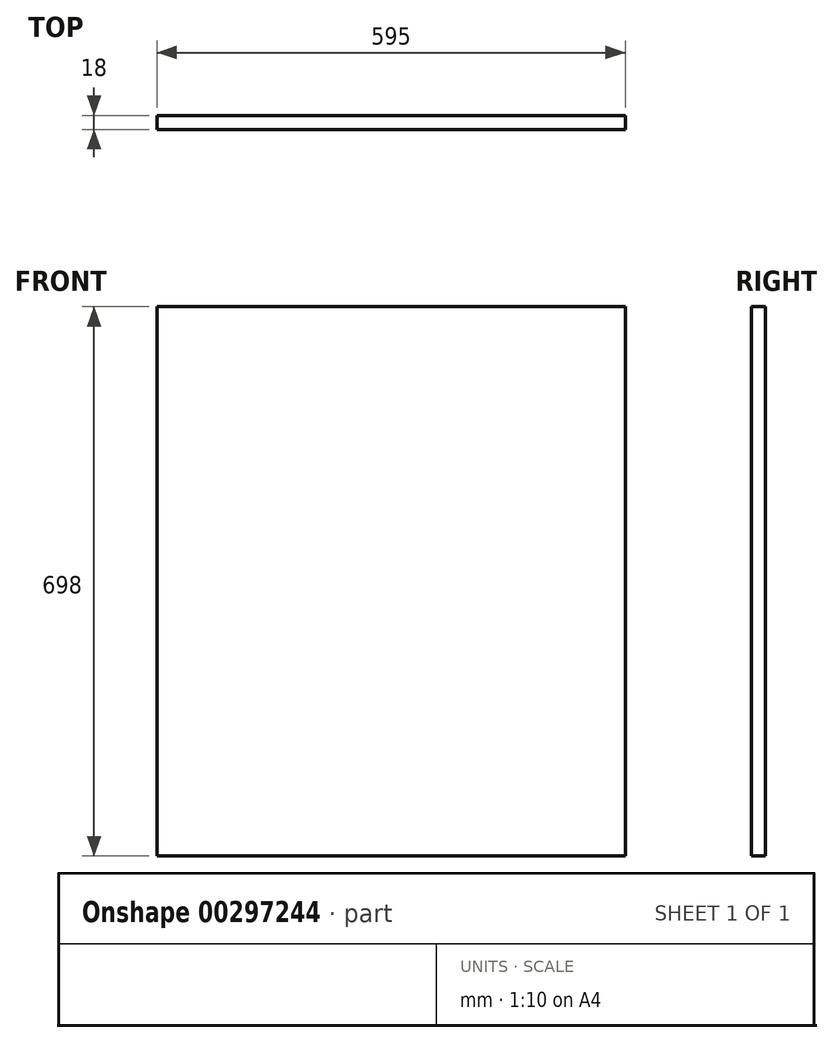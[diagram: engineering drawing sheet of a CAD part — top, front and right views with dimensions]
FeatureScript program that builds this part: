
annotation { "Feature Type Name" : "Feature", "Feature Type Description" : "" }
export const myFeature = defineFeature(function(context is Context, id is Id, definition is map)
    precondition{}
    {
        {
            var Q0;
            Q0=qCreatedBy(makeId("Front.planeOp"),FACE);
            var sketch = newSketch(context, id + "F0", { "sketchPlane" : qUnion([Q0])});
            skLineSegment(sketch, "E0.bottom", {"start": v(297.5, 349) * mm, "end": v(-297.5, 349) * mm});
            skLineSegment(sketch, "E0.top", {"start": v(297.5, -349) * mm, "end": v(-297.5, -349) * mm});
            skLineSegment(sketch, "E0.left", {"start": v(297.5, 349) * mm, "end": v(297.5, -349) * mm});
            skLineSegment(sketch, "E0.right", {"start": v(-297.5, 349) * mm, "end": v(-297.5, -349) * mm});
            skPoint(sketch, "E0.middle", {"position": v(0, 0) * mm});
            skSolve(sketch);
        }
        {
            var Q0;
            Q0 = qSketchRegion(id + "F0", true);
            extrude(context, id + "F1", {"entities" : qUnion([Q0]), "depth" : 18 * mm});
        }
    });
